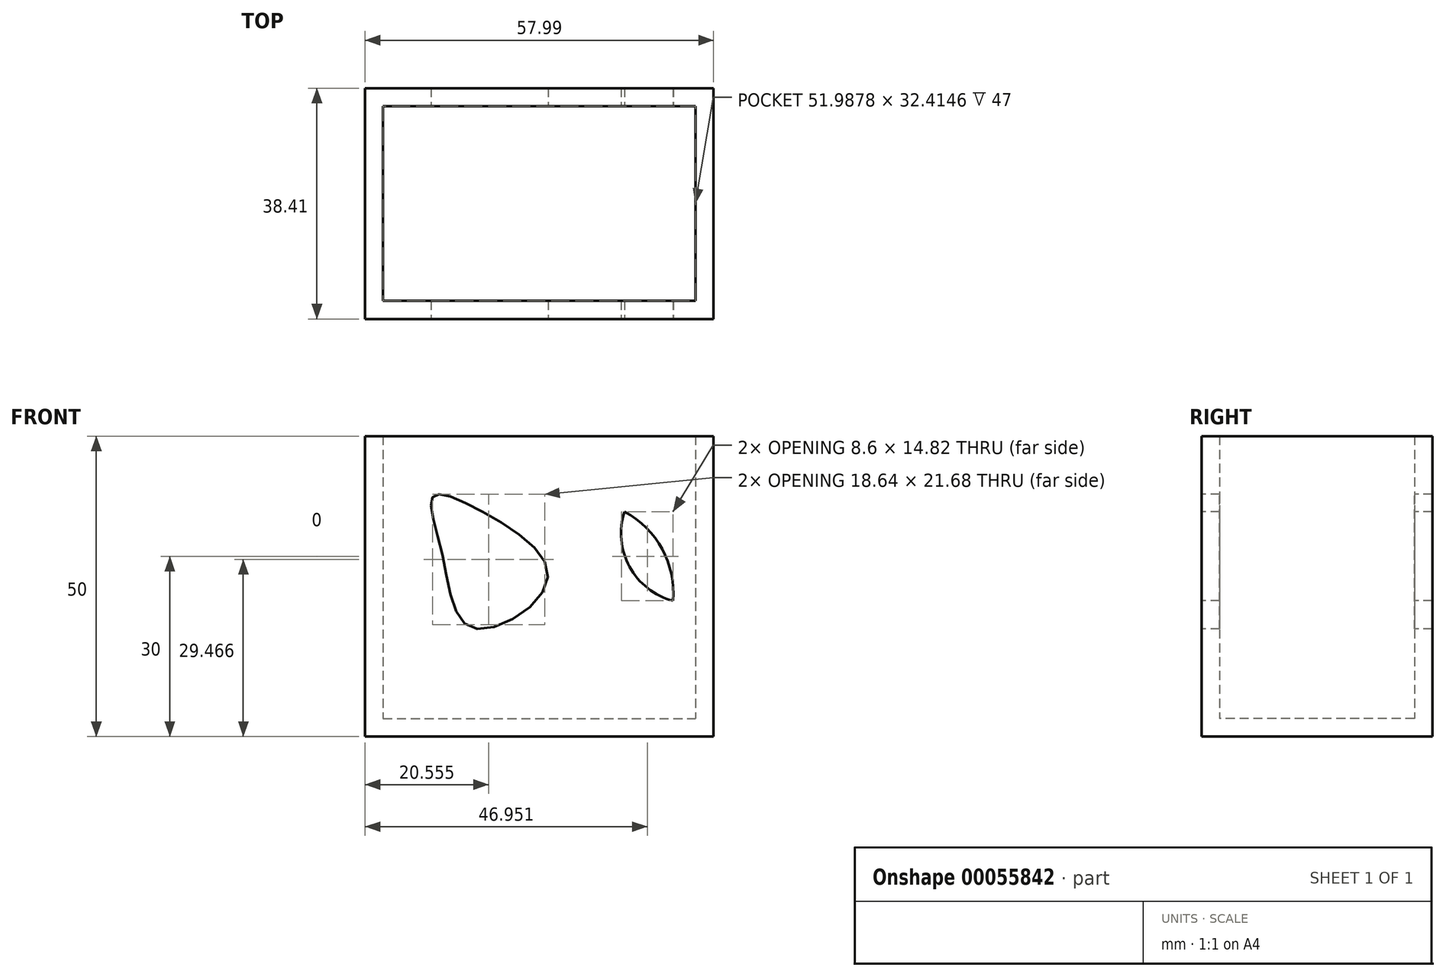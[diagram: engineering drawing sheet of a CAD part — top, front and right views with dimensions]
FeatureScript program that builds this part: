
annotation { "Feature Type Name" : "Feature", "Feature Type Description" : "" }
export const myFeature = defineFeature(function(context is Context, id is Id, definition is map)
    precondition{}
    {
        {
            var Q0;
            Q0=qCreatedBy(makeId("Top.planeOp"),FACE);
            var sketch = newSketch(context, id + "F0", { "sketchPlane" : qUnion([Q0])});
            skLineSegment(sketch, "E0.bottom", {"start": v(-36.04, 20.76) * mm, "end": v(21.95, 20.76) * mm});
            skLineSegment(sketch, "E0.top", {"start": v(-36.04, -17.65) * mm, "end": v(21.95, -17.65) * mm});
            skLineSegment(sketch, "E0.left", {"start": v(-36.04, 20.76) * mm, "end": v(-36.04, -17.65) * mm});
            skLineSegment(sketch, "E0.right", {"start": v(21.95, 20.76) * mm, "end": v(21.95, -17.65) * mm});
            skSolve(sketch);
        }
        {
            var Q0;
            Q0=makeQuery(id+"F0.imprint","IMPRINT",FACE,{"disambiguationData":[TD([[makeQuery(id+"F0.imprint","IMPRINT",EDGE,{"derivedFrom":sQuery(id+"F0.wireOp",EDGE,"E0.bottom")}),-1.0]])]});
            extrude(context, id + "F1", {"entities" : qUnion([Q0]), "depth" : 50 * mm});
        }
        {
            var Q0;
            Q0=makeQuery(id+"F1.opExtrude","CAP_FACE",FACE,{"disambiguationData":[OSD([sQuery(id+"F0.wireOp",EDGE,"E0.bottom"),sQuery(id+"F0.wireOp",EDGE,"E0.top"),sQuery(id+"F0.wireOp",EDGE,"E0.left"),sQuery(id+"F0.wireOp",EDGE,"E0.right")])],"isStart":false});
            shell(context, id + "F2", {"entities" : qUnion([Q0]), "thickness" : 3 * mm});
        }
        {
            var Q0;
            Q0=makeQuery(id+"F1.opExtrude","SWEPT_FACE",FACE,{"disambiguationData":[OSD([sQuery(id+"F0.wireOp",EDGE,"E0.top")])]});
            var sketch = newSketch(context, id + "F3", { "sketchPlane" : qUnion([Q0])});
            skFitSpline(sketch, "E1", {"points": [v(-16.46, 37.4) * mm, v(-5.67, 26.07) * mm, v(-17.93, 18.02) * mm, v(-23.23, 30.46) * mm, v(-24.7, 39.97) * mm, v(-16.46, 37.4) * mm]});
            skArc(sketch, "E2", {"start": v(7.13, 37.4) * mm, "mid": v(7.97, 28.27) * mm, "end": v(15.18, 22.6) * mm});
            skArc(sketch, "E3", {"start": v(15.18, 22.6) * mm, "mid": v(13.39, 31.21) * mm, "end": v(7.13, 37.4) * mm});
            skSolve(sketch);
        }
        {
            var Q0;
            Q0 = qSketchRegion(id + "F3", true);
            extrude(context, id + "F4", {"entities" : qUnion([Q0]), "operationType" : NewBodyOperationType.REMOVE, "endBound" : BoundingType.THROUGH_ALL, "oppositeDirection" : true, "depth" : 25 * mm});
        }
    });
